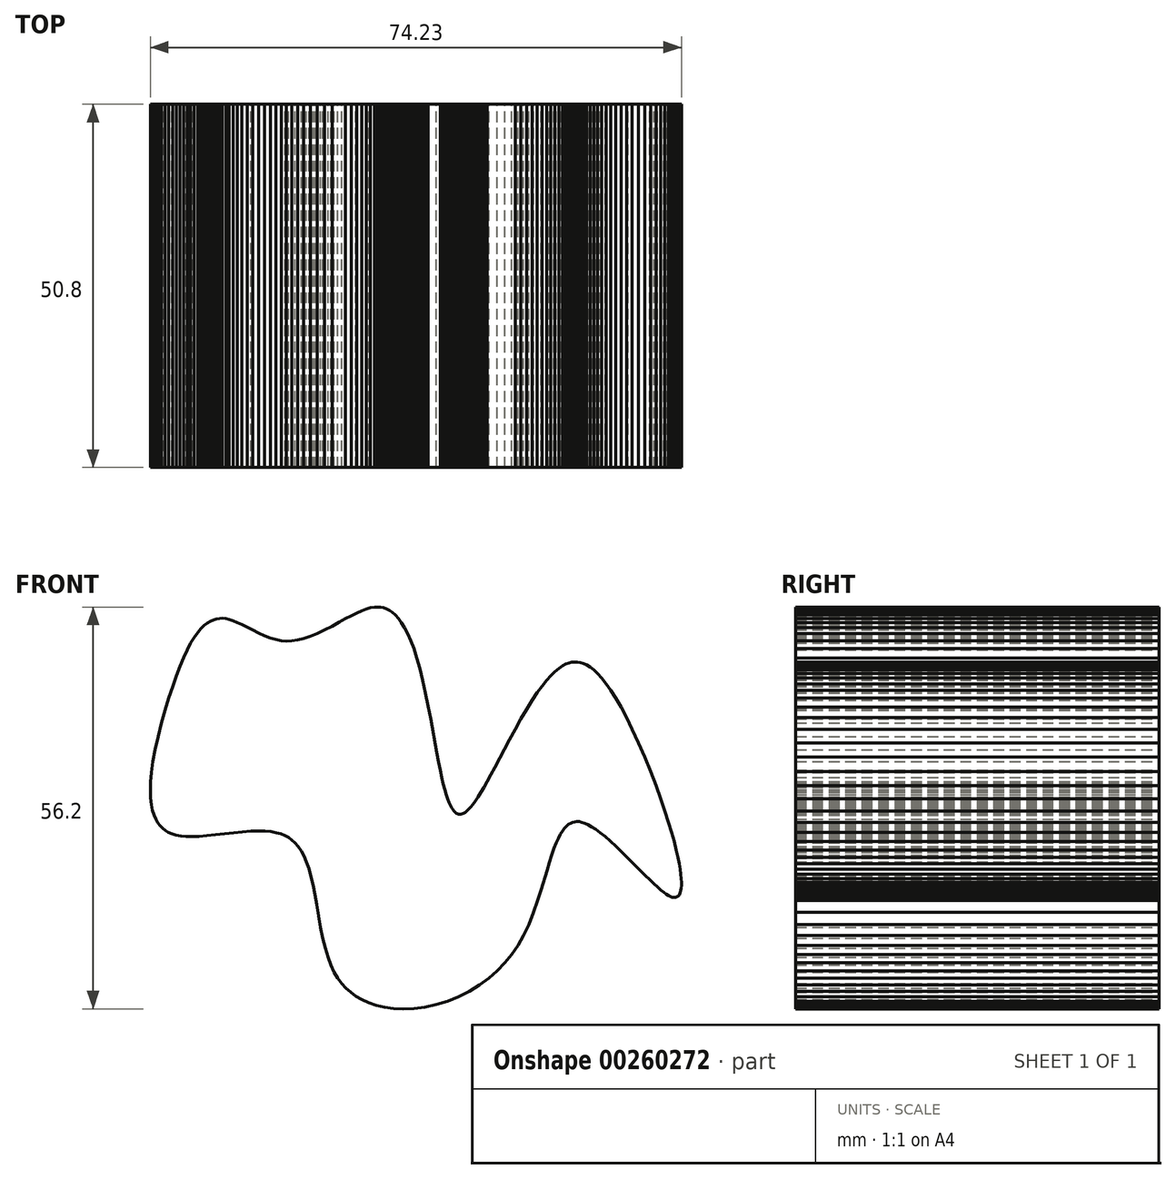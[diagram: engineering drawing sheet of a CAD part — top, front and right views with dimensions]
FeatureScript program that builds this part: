
annotation { "Feature Type Name" : "Feature", "Feature Type Description" : "" }
export const myFeature = defineFeature(function(context is Context, id is Id, definition is map)
    precondition{}
    {
        {
            var Q0;
            Q0=qCreatedBy(makeId("Front.planeOp"),FACE);
            var sketch = newSketch(context, id + "F0", { "sketchPlane" : qUnion([Q0])});
            skLineSegment(sketch, "E0", {"start": v(-36.64, -3.62) * mm, "end": v(-35.67, -3.6) * mm});
            skLineSegment(sketch, "E1", {"start": v(-35.67, -3.6) * mm, "end": v(-34.6, -3.51) * mm});
            skLineSegment(sketch, "E2", {"start": v(-34.6, -3.51) * mm, "end": v(-33.42, -3.4) * mm});
            skLineSegment(sketch, "E3", {"start": v(-33.42, -3.4) * mm, "end": v(-30.87, -3.1) * mm});
            skLineSegment(sketch, "E4", {"start": v(-30.87, -3.1) * mm, "end": v(-29.63, -2.97) * mm});
            skLineSegment(sketch, "E5", {"start": v(-29.63, -2.97) * mm, "end": v(-28.47, -2.89) * mm});
            skLineSegment(sketch, "E6", {"start": v(-28.47, -2.89) * mm, "end": v(-27.42, -2.85) * mm});
            skLineSegment(sketch, "E7", {"start": v(-27.42, -2.85) * mm, "end": v(-26.48, -2.88) * mm});
            skLineSegment(sketch, "E8", {"start": v(-26.48, -2.88) * mm, "end": v(-25.64, -2.96) * mm});
            skLineSegment(sketch, "E9", {"start": v(-25.64, -2.96) * mm, "end": v(-24.9, -3.09) * mm});
            skLineSegment(sketch, "E10", {"start": v(-24.9, -3.09) * mm, "end": v(-24.25, -3.27) * mm});
            skLineSegment(sketch, "E11", {"start": v(-24.25, -3.27) * mm, "end": v(-23.68, -3.5) * mm});
            skLineSegment(sketch, "E12", {"start": v(-23.68, -3.5) * mm, "end": v(-23.18, -3.78) * mm});
            skLineSegment(sketch, "E13", {"start": v(-23.18, -3.78) * mm, "end": v(-22.71, -4.12) * mm});
            skLineSegment(sketch, "E14", {"start": v(-22.71, -4.12) * mm, "end": v(-22.26, -4.53) * mm});
            skLineSegment(sketch, "E15", {"start": v(-22.26, -4.53) * mm, "end": v(-21.84, -5.03) * mm});
            skLineSegment(sketch, "E16", {"start": v(-21.84, -5.03) * mm, "end": v(-21.43, -5.63) * mm});
            skLineSegment(sketch, "E17", {"start": v(-21.43, -5.63) * mm, "end": v(-21.05, -6.34) * mm});
            skLineSegment(sketch, "E18", {"start": v(-21.05, -6.34) * mm, "end": v(-20.69, -7.17) * mm});
            skLineSegment(sketch, "E19", {"start": v(-20.69, -7.17) * mm, "end": v(-20.36, -8.12) * mm});
            skLineSegment(sketch, "E20", {"start": v(-20.36, -8.12) * mm, "end": v(-20.06, -9.2) * mm});
            skLineSegment(sketch, "E21", {"start": v(-20.06, -9.2) * mm, "end": v(-19.78, -10.4) * mm});
            skLineSegment(sketch, "E22", {"start": v(-19.78, -10.4) * mm, "end": v(-19.52, -11.73) * mm});
            skLineSegment(sketch, "E23", {"start": v(-19.52, -11.73) * mm, "end": v(-19.26, -13.17) * mm});
            skLineSegment(sketch, "E24", {"start": v(-19.26, -13.17) * mm, "end": v(-19, -14.74) * mm});
            skLineSegment(sketch, "E25", {"start": v(-19, -14.74) * mm, "end": v(-18.72, -16.33) * mm});
            skLineSegment(sketch, "E26", {"start": v(-18.72, -16.33) * mm, "end": v(-18.4, -17.84) * mm});
            skLineSegment(sketch, "E27", {"start": v(-18.4, -17.84) * mm, "end": v(-18.07, -19.25) * mm});
            skLineSegment(sketch, "E28", {"start": v(-18.07, -19.25) * mm, "end": v(-17.69, -20.5) * mm});
            skLineSegment(sketch, "E29", {"start": v(-17.69, -20.5) * mm, "end": v(-17.27, -21.62) * mm});
            skLineSegment(sketch, "E30", {"start": v(-17.27, -21.62) * mm, "end": v(-16.8, -22.6) * mm});
            skLineSegment(sketch, "E31", {"start": v(-16.8, -22.6) * mm, "end": v(-16.3, -23.45) * mm});
            skLineSegment(sketch, "E32", {"start": v(-16.3, -23.45) * mm, "end": v(-15.77, -24.18) * mm});
            skLineSegment(sketch, "E33", {"start": v(-15.77, -24.18) * mm, "end": v(-15.18, -24.83) * mm});
            skLineSegment(sketch, "E34", {"start": v(-15.18, -24.83) * mm, "end": v(-14.52, -25.42) * mm});
            skLineSegment(sketch, "E35", {"start": v(-14.52, -25.42) * mm, "end": v(-13.77, -25.96) * mm});
            skLineSegment(sketch, "E36", {"start": v(-13.77, -25.96) * mm, "end": v(-12.94, -26.44) * mm});
            skLineSegment(sketch, "E37", {"start": v(-12.94, -26.44) * mm, "end": v(-12, -26.87) * mm});
            skLineSegment(sketch, "E38", {"start": v(-12, -26.87) * mm, "end": v(-10.95, -27.22) * mm});
            skLineSegment(sketch, "E39", {"start": v(-10.95, -27.22) * mm, "end": v(-9.8, -27.5) * mm});
            skLineSegment(sketch, "E40", {"start": v(-9.8, -27.5) * mm, "end": v(-8.53, -27.67) * mm});
            skLineSegment(sketch, "E41", {"start": v(-8.53, -27.67) * mm, "end": v(-7.16, -27.73) * mm});
            skLineSegment(sketch, "E42", {"start": v(-7.16, -27.73) * mm, "end": v(-5.69, -27.67) * mm});
            skLineSegment(sketch, "E43", {"start": v(-5.69, -27.67) * mm, "end": v(-4.15, -27.48) * mm});
            skLineSegment(sketch, "E44", {"start": v(-4.15, -27.48) * mm, "end": v(-2.57, -27.14) * mm});
            skLineSegment(sketch, "E45", {"start": v(-2.57, -27.14) * mm, "end": v(-0.99, -26.65) * mm});
            skLineSegment(sketch, "E46", {"start": v(-0.99, -26.65) * mm, "end": v(0.57, -26.03) * mm});
            skLineSegment(sketch, "E47", {"start": v(0.57, -26.03) * mm, "end": v(2.07, -25.28) * mm});
            skLineSegment(sketch, "E48", {"start": v(2.07, -25.28) * mm, "end": v(3.48, -24.42) * mm});
            skLineSegment(sketch, "E49", {"start": v(3.48, -24.42) * mm, "end": v(4.8, -23.46) * mm});
            skLineSegment(sketch, "E50", {"start": v(4.8, -23.46) * mm, "end": v(5.98, -22.42) * mm});
            skLineSegment(sketch, "E51", {"start": v(5.98, -22.42) * mm, "end": v(7.06, -21.3) * mm});
            skLineSegment(sketch, "E52", {"start": v(7.06, -21.3) * mm, "end": v(8, -20.15) * mm});
            skLineSegment(sketch, "E53", {"start": v(8, -20.15) * mm, "end": v(8.85, -18.89) * mm});
            skLineSegment(sketch, "E54", {"start": v(8.85, -18.89) * mm, "end": v(9.65, -17.46) * mm});
            skLineSegment(sketch, "E55", {"start": v(9.65, -17.46) * mm, "end": v(10.38, -15.92) * mm});
            skLineSegment(sketch, "E56", {"start": v(10.38, -15.92) * mm, "end": v(11.04, -14.24) * mm});
            skLineSegment(sketch, "E57", {"start": v(11.04, -14.24) * mm, "end": v(11.63, -12.57) * mm});
            skLineSegment(sketch, "E58", {"start": v(11.63, -12.57) * mm, "end": v(12.12, -11.04) * mm});
            skLineSegment(sketch, "E59", {"start": v(12.12, -11.04) * mm, "end": v(12.92, -8.36) * mm});
            skLineSegment(sketch, "E60", {"start": v(-3.33, 12.8) * mm, "end": v(-3.67, 14.58) * mm});
            skLineSegment(sketch, "E61", {"start": v(-3.67, 14.58) * mm, "end": v(-4.05, 16.43) * mm});
            skLineSegment(sketch, "E62", {"start": v(-4.05, 16.43) * mm, "end": v(-4.45, 18.24) * mm});
            skLineSegment(sketch, "E63", {"start": v(-4.45, 18.24) * mm, "end": v(-4.85, 19.87) * mm});
            skLineSegment(sketch, "E64", {"start": v(-4.85, 19.87) * mm, "end": v(-5.27, 21.34) * mm});
            skLineSegment(sketch, "E65", {"start": v(-5.27, 21.34) * mm, "end": v(-5.7, 22.63) * mm});
            skLineSegment(sketch, "E66", {"start": v(-5.7, 22.63) * mm, "end": v(-6.12, 23.77) * mm});
            skLineSegment(sketch, "E67", {"start": v(-6.12, 23.77) * mm, "end": v(-6.55, 24.75) * mm});
            skLineSegment(sketch, "E68", {"start": v(-6.55, 24.75) * mm, "end": v(-6.98, 25.58) * mm});
            skLineSegment(sketch, "E69", {"start": v(-6.98, 25.58) * mm, "end": v(-7.4, 26.29) * mm});
            skLineSegment(sketch, "E70", {"start": v(-7.4, 26.29) * mm, "end": v(-7.84, 26.87) * mm});
            skLineSegment(sketch, "E71", {"start": v(-7.84, 26.87) * mm, "end": v(-8.26, 27.35) * mm});
            skLineSegment(sketch, "E72", {"start": v(-8.26, 27.35) * mm, "end": v(-8.68, 27.72) * mm});
            skLineSegment(sketch, "E73", {"start": v(-8.68, 27.72) * mm, "end": v(-9.09, 28) * mm});
            skLineSegment(sketch, "E74", {"start": v(-9.09, 28) * mm, "end": v(-9.5, 28.21) * mm});
            skLineSegment(sketch, "E75", {"start": v(-9.5, 28.21) * mm, "end": v(-9.89, 28.36) * mm});
            skLineSegment(sketch, "E76", {"start": v(-9.89, 28.36) * mm, "end": v(-10.3, 28.44) * mm});
            skLineSegment(sketch, "E77", {"start": v(-10.3, 28.44) * mm, "end": v(-10.73, 28.47) * mm});
            skLineSegment(sketch, "E78", {"start": v(-10.73, 28.47) * mm, "end": v(-11.2, 28.45) * mm});
            skLineSegment(sketch, "E79", {"start": v(-11.2, 28.45) * mm, "end": v(-11.73, 28.35) * mm});
            skLineSegment(sketch, "E80", {"start": v(-11.73, 28.35) * mm, "end": v(-12.31, 28.19) * mm});
            skLineSegment(sketch, "E81", {"start": v(-12.31, 28.19) * mm, "end": v(-12.95, 27.95) * mm});
            skLineSegment(sketch, "E82", {"start": v(-12.95, 27.95) * mm, "end": v(-13.65, 27.65) * mm});
            skLineSegment(sketch, "E83", {"start": v(-13.65, 27.65) * mm, "end": v(-14.42, 27.27) * mm});
            skLineSegment(sketch, "E84", {"start": v(-14.42, 27.27) * mm, "end": v(-15.25, 26.83) * mm});
            skLineSegment(sketch, "E85", {"start": v(-15.25, 26.83) * mm, "end": v(-16.16, 26.33) * mm});
            skLineSegment(sketch, "E86", {"start": v(-16.16, 26.33) * mm, "end": v(-17.12, 25.8) * mm});
            skLineSegment(sketch, "E87", {"start": v(-17.12, 25.8) * mm, "end": v(-18.14, 25.27) * mm});
            skLineSegment(sketch, "E88", {"start": v(-18.14, 25.27) * mm, "end": v(-19.17, 24.77) * mm});
            skLineSegment(sketch, "E89", {"start": v(-19.17, 24.77) * mm, "end": v(-20.15, 24.37) * mm});
            skLineSegment(sketch, "E90", {"start": v(-20.15, 24.37) * mm, "end": v(-21.07, 24.06) * mm});
            skLineSegment(sketch, "E91", {"start": v(-21.07, 24.06) * mm, "end": v(-21.93, 23.85) * mm});
            skLineSegment(sketch, "E92", {"start": v(-21.93, 23.85) * mm, "end": v(-22.74, 23.74) * mm});
            skLineSegment(sketch, "E93", {"start": v(-22.74, 23.74) * mm, "end": v(-23.5, 23.7) * mm});
            skLineSegment(sketch, "E94", {"start": v(-23.5, 23.7) * mm, "end": v(-24.22, 23.77) * mm});
            skLineSegment(sketch, "E95", {"start": v(-24.22, 23.77) * mm, "end": v(-24.96, 23.9) * mm});
            skLineSegment(sketch, "E96", {"start": v(-24.96, 23.9) * mm, "end": v(-25.72, 24.14) * mm});
            skLineSegment(sketch, "E97", {"start": v(-25.72, 24.14) * mm, "end": v(-26.53, 24.45) * mm});
            skLineSegment(sketch, "E98", {"start": v(-26.53, 24.45) * mm, "end": v(-27.37, 24.83) * mm});
            skLineSegment(sketch, "E99", {"start": v(-27.37, 24.83) * mm, "end": v(-28.2, 25.24) * mm});
            skLineSegment(sketch, "E100", {"start": v(-28.2, 25.24) * mm, "end": v(-28.98, 25.65) * mm});
            skLineSegment(sketch, "E101", {"start": v(-28.98, 25.65) * mm, "end": v(-29.7, 26) * mm});
            skLineSegment(sketch, "E102", {"start": v(-29.7, 26) * mm, "end": v(-30.34, 26.3) * mm});
            skLineSegment(sketch, "E103", {"start": v(-30.34, 26.3) * mm, "end": v(-30.94, 26.55) * mm});
            skLineSegment(sketch, "E104", {"start": v(-30.94, 26.55) * mm, "end": v(-31.48, 26.72) * mm});
            skLineSegment(sketch, "E105", {"start": v(-31.48, 26.72) * mm, "end": v(-31.98, 26.84) * mm});
            skLineSegment(sketch, "E106", {"start": v(-31.98, 26.84) * mm, "end": v(-32.43, 26.89) * mm});
            skLineSegment(sketch, "E107", {"start": v(-2.48, 8.11) * mm, "end": v(-3.33, 12.8) * mm});
            skLineSegment(sketch, "E108", {"start": v(5.65, 6.05) * mm, "end": v(5.08, 5) * mm});
            skLineSegment(sketch, "E109", {"start": v(5.08, 5) * mm, "end": v(4.57, 4.06) * mm});
            skLineSegment(sketch, "E110", {"start": v(4.57, 4.06) * mm, "end": v(4.1, 3.23) * mm});
            skLineSegment(sketch, "E111", {"start": v(4.1, 3.23) * mm, "end": v(3.66, 2.5) * mm});
            skLineSegment(sketch, "E112", {"start": v(3.66, 2.5) * mm, "end": v(3.26, 1.88) * mm});
            skLineSegment(sketch, "E113", {"start": v(3.26, 1.88) * mm, "end": v(2.9, 1.34) * mm});
            skLineSegment(sketch, "E114", {"start": v(2.9, 1.34) * mm, "end": v(2.57, 0.89) * mm});
            skLineSegment(sketch, "E115", {"start": v(2.57, 0.89) * mm, "end": v(2.26, 0.5) * mm});
            skLineSegment(sketch, "E116", {"start": v(2.26, 0.5) * mm, "end": v(1.98, 0.2) * mm});
            skLineSegment(sketch, "E117", {"start": v(1.98, 0.2) * mm, "end": v(1.73, -0.04) * mm});
            skLineSegment(sketch, "E118", {"start": v(1.73, -0.04) * mm, "end": v(1.5, -0.23) * mm});
            skLineSegment(sketch, "E119", {"start": v(1.5, -0.23) * mm, "end": v(1.28, -0.36) * mm});
            skLineSegment(sketch, "E120", {"start": v(1.28, -0.36) * mm, "end": v(1.09, -0.45) * mm});
            skLineSegment(sketch, "E121", {"start": v(1.09, -0.45) * mm, "end": v(0.9, -0.5) * mm});
            skLineSegment(sketch, "E122", {"start": v(0.9, -0.5) * mm, "end": v(0.74, -0.52) * mm});
            skLineSegment(sketch, "E123", {"start": v(0.74, -0.52) * mm, "end": v(0.58, -0.5) * mm});
            skLineSegment(sketch, "E124", {"start": v(0.58, -0.5) * mm, "end": v(0.43, -0.46) * mm});
            skLineSegment(sketch, "E125", {"start": v(0.43, -0.46) * mm, "end": v(0.27, -0.38) * mm});
            skLineSegment(sketch, "E126", {"start": v(0.27, -0.38) * mm, "end": v(0.1, -0.26) * mm});
            skLineSegment(sketch, "E127", {"start": v(0.1, -0.26) * mm, "end": v(-0.06, -0.1) * mm});
            skLineSegment(sketch, "E128", {"start": v(-0.06, -0.1) * mm, "end": v(-0.23, 0.13) * mm});
            skLineSegment(sketch, "E129", {"start": v(-0.23, 0.13) * mm, "end": v(-0.4, 0.4) * mm});
            skLineSegment(sketch, "E130", {"start": v(-0.4, 0.4) * mm, "end": v(-0.59, 0.75) * mm});
            skLineSegment(sketch, "E131", {"start": v(-0.59, 0.75) * mm, "end": v(-0.77, 1.16) * mm});
            skLineSegment(sketch, "E132", {"start": v(-0.77, 1.16) * mm, "end": v(-0.96, 1.66) * mm});
            skLineSegment(sketch, "E133", {"start": v(-0.96, 1.66) * mm, "end": v(-1.16, 2.25) * mm});
            skLineSegment(sketch, "E134", {"start": v(-1.16, 2.25) * mm, "end": v(-1.36, 2.93) * mm});
            skLineSegment(sketch, "E135", {"start": v(-1.36, 2.93) * mm, "end": v(-1.56, 3.72) * mm});
            skLineSegment(sketch, "E136", {"start": v(-1.56, 3.72) * mm, "end": v(-1.78, 4.63) * mm});
            skLineSegment(sketch, "E137", {"start": v(-1.78, 4.63) * mm, "end": v(-2, 5.66) * mm});
            skLineSegment(sketch, "E138", {"start": v(-2, 5.66) * mm, "end": v(-2.23, 6.82) * mm});
            skLineSegment(sketch, "E139", {"start": v(-2.23, 6.82) * mm, "end": v(-2.48, 8.11) * mm});
            skLineSegment(sketch, "E140", {"start": v(24.28, -6.68) * mm, "end": v(25.95, -8.37) * mm});
            skLineSegment(sketch, "E141", {"start": v(25.95, -8.37) * mm, "end": v(26.64, -9.06) * mm});
            skLineSegment(sketch, "E142", {"start": v(26.64, -9.06) * mm, "end": v(27.28, -9.69) * mm});
            skLineSegment(sketch, "E143", {"start": v(27.28, -9.69) * mm, "end": v(27.85, -10.23) * mm});
            skLineSegment(sketch, "E144", {"start": v(27.85, -10.23) * mm, "end": v(28.37, -10.7) * mm});
            skLineSegment(sketch, "E145", {"start": v(28.37, -10.7) * mm, "end": v(28.83, -11.1) * mm});
            skLineSegment(sketch, "E146", {"start": v(28.83, -11.1) * mm, "end": v(29.23, -11.42) * mm});
            skLineSegment(sketch, "E147", {"start": v(29.23, -11.42) * mm, "end": v(29.6, -11.68) * mm});
            skLineSegment(sketch, "E148", {"start": v(29.6, -11.68) * mm, "end": v(29.9, -11.87) * mm});
            skLineSegment(sketch, "E149", {"start": v(29.9, -11.87) * mm, "end": v(30.18, -12.01) * mm});
            skLineSegment(sketch, "E150", {"start": v(30.18, -12.01) * mm, "end": v(30.41, -12.1) * mm});
            skLineSegment(sketch, "E151", {"start": v(30.41, -12.1) * mm, "end": v(30.61, -12.15) * mm});
            skLineSegment(sketch, "E152", {"start": v(30.61, -12.15) * mm, "end": v(30.79, -12.16) * mm});
            skLineSegment(sketch, "E153", {"start": v(30.79, -12.16) * mm, "end": v(30.93, -12.14) * mm});
            skLineSegment(sketch, "E154", {"start": v(30.93, -12.14) * mm, "end": v(31.07, -12.1) * mm});
            skLineSegment(sketch, "E155", {"start": v(31.07, -12.1) * mm, "end": v(31.19, -12.03) * mm});
            skLineSegment(sketch, "E156", {"start": v(31.19, -12.03) * mm, "end": v(31.3, -11.93) * mm});
            skLineSegment(sketch, "E157", {"start": v(31.3, -11.93) * mm, "end": v(31.4, -11.8) * mm});
            skLineSegment(sketch, "E158", {"start": v(31.4, -11.8) * mm, "end": v(31.49, -11.64) * mm});
            skLineSegment(sketch, "E159", {"start": v(31.49, -11.64) * mm, "end": v(31.57, -11.43) * mm});
            skLineSegment(sketch, "E160", {"start": v(31.57, -11.43) * mm, "end": v(31.63, -11.17) * mm});
            skLineSegment(sketch, "E161", {"start": v(31.63, -11.17) * mm, "end": v(31.68, -10.85) * mm});
            skLineSegment(sketch, "E162", {"start": v(31.68, -10.85) * mm, "end": v(31.7, -10.48) * mm});
            skLineSegment(sketch, "E163", {"start": v(31.7, -10.48) * mm, "end": v(31.71, -10.03) * mm});
            skLineSegment(sketch, "E164", {"start": v(31.71, -10.03) * mm, "end": v(31.69, -9.52) * mm});
            skLineSegment(sketch, "E165", {"start": v(31.69, -9.52) * mm, "end": v(31.63, -8.91) * mm});
            skLineSegment(sketch, "E166", {"start": v(31.63, -8.91) * mm, "end": v(31.54, -8.22) * mm});
            skLineSegment(sketch, "E167", {"start": v(31.54, -8.22) * mm, "end": v(31.4, -7.43) * mm});
            skLineSegment(sketch, "E168", {"start": v(31.4, -7.43) * mm, "end": v(31.22, -6.52) * mm});
            skLineSegment(sketch, "E169", {"start": v(31.22, -6.52) * mm, "end": v(30.99, -5.5) * mm});
            skLineSegment(sketch, "E170", {"start": v(30.99, -5.5) * mm, "end": v(30.7, -4.35) * mm});
            skLineSegment(sketch, "E171", {"start": v(30.7, -4.35) * mm, "end": v(30.34, -3.06) * mm});
            skLineSegment(sketch, "E172", {"start": v(30.34, -3.06) * mm, "end": v(29.91, -1.63) * mm});
            skLineSegment(sketch, "E173", {"start": v(29.91, -1.63) * mm, "end": v(29.4, -0.06) * mm});
            skLineSegment(sketch, "E174", {"start": v(29.4, -0.06) * mm, "end": v(28.82, 1.65) * mm});
            skLineSegment(sketch, "E175", {"start": v(28.82, 1.65) * mm, "end": v(28.15, 3.49) * mm});
            skLineSegment(sketch, "E176", {"start": v(28.15, 3.49) * mm, "end": v(27.4, 5.46) * mm});
            skLineSegment(sketch, "E177", {"start": v(27.4, 5.46) * mm, "end": v(26.57, 7.48) * mm});
            skLineSegment(sketch, "E178", {"start": v(26.57, 7.48) * mm, "end": v(25.7, 9.48) * mm});
            skLineSegment(sketch, "E179", {"start": v(25.7, 9.48) * mm, "end": v(24.84, 11.36) * mm});
            skLineSegment(sketch, "E180", {"start": v(24.84, 11.36) * mm, "end": v(24.03, 13) * mm});
            skLineSegment(sketch, "E181", {"start": v(24.03, 13) * mm, "end": v(23.27, 14.46) * mm});
            skLineSegment(sketch, "E182", {"start": v(23.27, 14.46) * mm, "end": v(22.54, 15.72) * mm});
            skLineSegment(sketch, "E183", {"start": v(22.54, 15.72) * mm, "end": v(21.86, 16.81) * mm});
            skLineSegment(sketch, "E184", {"start": v(21.86, 16.81) * mm, "end": v(21.2, 17.74) * mm});
            skLineSegment(sketch, "E185", {"start": v(21.2, 17.74) * mm, "end": v(20.6, 18.51) * mm});
            skLineSegment(sketch, "E186", {"start": v(20.6, 18.51) * mm, "end": v(20.01, 19.15) * mm});
            skLineSegment(sketch, "E187", {"start": v(12.92, -8.36) * mm, "end": v(13.27, -7.21) * mm});
            skLineSegment(sketch, "E188", {"start": v(13.27, -7.21) * mm, "end": v(13.6, -6.2) * mm});
            skLineSegment(sketch, "E189", {"start": v(13.6, -6.2) * mm, "end": v(13.9, -5.3) * mm});
            skLineSegment(sketch, "E190", {"start": v(13.9, -5.3) * mm, "end": v(14.2, -4.53) * mm});
            skLineSegment(sketch, "E191", {"start": v(14.2, -4.53) * mm, "end": v(14.5, -3.86) * mm});
            skLineSegment(sketch, "E192", {"start": v(14.5, -3.86) * mm, "end": v(14.8, -3.3) * mm});
            skLineSegment(sketch, "E193", {"start": v(14.8, -3.3) * mm, "end": v(15.09, -2.83) * mm});
            skLineSegment(sketch, "E194", {"start": v(15.09, -2.83) * mm, "end": v(15.38, -2.45) * mm});
            skLineSegment(sketch, "E195", {"start": v(15.38, -2.45) * mm, "end": v(15.66, -2.15) * mm});
            skLineSegment(sketch, "E196", {"start": v(15.66, -2.15) * mm, "end": v(15.94, -1.92) * mm});
            skLineSegment(sketch, "E197", {"start": v(15.94, -1.92) * mm, "end": v(16.23, -1.75) * mm});
            skLineSegment(sketch, "E198", {"start": v(16.23, -1.75) * mm, "end": v(16.5, -1.63) * mm});
            skLineSegment(sketch, "E199", {"start": v(16.5, -1.63) * mm, "end": v(16.8, -1.56) * mm});
            skLineSegment(sketch, "E200", {"start": v(16.8, -1.56) * mm, "end": v(17.1, -1.54) * mm});
            skLineSegment(sketch, "E201", {"start": v(17.1, -1.54) * mm, "end": v(17.42, -1.56) * mm});
            skLineSegment(sketch, "E202", {"start": v(17.42, -1.56) * mm, "end": v(17.8, -1.63) * mm});
            skLineSegment(sketch, "E203", {"start": v(17.8, -1.63) * mm, "end": v(18.2, -1.77) * mm});
            skLineSegment(sketch, "E204", {"start": v(18.2, -1.77) * mm, "end": v(18.66, -1.98) * mm});
            skLineSegment(sketch, "E205", {"start": v(18.66, -1.98) * mm, "end": v(19.18, -2.27) * mm});
            skLineSegment(sketch, "E206", {"start": v(19.18, -2.27) * mm, "end": v(19.74, -2.64) * mm});
            skLineSegment(sketch, "E207", {"start": v(19.74, -2.64) * mm, "end": v(20.37, -3.1) * mm});
            skLineSegment(sketch, "E208", {"start": v(20.37, -3.1) * mm, "end": v(21.05, -3.65) * mm});
            skLineSegment(sketch, "E209", {"start": v(21.05, -3.65) * mm, "end": v(21.78, -4.29) * mm});
            skLineSegment(sketch, "E210", {"start": v(21.78, -4.29) * mm, "end": v(22.57, -5.01) * mm});
            skLineSegment(sketch, "E211", {"start": v(22.57, -5.01) * mm, "end": v(23.4, -5.82) * mm});
            skLineSegment(sketch, "E212", {"start": v(23.4, -5.82) * mm, "end": v(24.28, -6.68) * mm});
            skLineSegment(sketch, "E213", {"start": v(-32.43, 26.89) * mm, "end": v(-32.85, 26.88) * mm});
            skLineSegment(sketch, "E214", {"start": v(-32.85, 26.88) * mm, "end": v(-33.27, 26.81) * mm});
            skLineSegment(sketch, "E215", {"start": v(-33.27, 26.81) * mm, "end": v(-33.68, 26.7) * mm});
            skLineSegment(sketch, "E216", {"start": v(-33.68, 26.7) * mm, "end": v(-34.1, 26.5) * mm});
            skLineSegment(sketch, "E217", {"start": v(-34.1, 26.5) * mm, "end": v(-34.54, 26.24) * mm});
            skLineSegment(sketch, "E218", {"start": v(-34.54, 26.24) * mm, "end": v(-34.98, 25.89) * mm});
            skLineSegment(sketch, "E219", {"start": v(-34.98, 25.89) * mm, "end": v(-35.44, 25.44) * mm});
            skLineSegment(sketch, "E220", {"start": v(-35.44, 25.44) * mm, "end": v(-35.91, 24.88) * mm});
            skLineSegment(sketch, "E221", {"start": v(-35.91, 24.88) * mm, "end": v(-36.39, 24.21) * mm});
            skLineSegment(sketch, "E222", {"start": v(-36.39, 24.21) * mm, "end": v(-36.88, 23.41) * mm});
            skLineSegment(sketch, "E223", {"start": v(-36.88, 23.41) * mm, "end": v(-37.37, 22.48) * mm});
            skLineSegment(sketch, "E224", {"start": v(-37.37, 22.48) * mm, "end": v(-37.87, 21.4) * mm});
            skLineSegment(sketch, "E225", {"start": v(-37.87, 21.4) * mm, "end": v(-38.37, 20.19) * mm});
            skLineSegment(sketch, "E226", {"start": v(-38.37, 20.19) * mm, "end": v(-38.89, 18.83) * mm});
            skLineSegment(sketch, "E227", {"start": v(-38.89, 18.83) * mm, "end": v(-39.4, 17.34) * mm});
            skLineSegment(sketch, "E228", {"start": v(-39.4, 17.34) * mm, "end": v(-39.92, 15.74) * mm});
            skLineSegment(sketch, "E229", {"start": v(-39.92, 15.74) * mm, "end": v(-40.45, 14.04) * mm});
            skLineSegment(sketch, "E230", {"start": v(-40.45, 14.04) * mm, "end": v(-40.95, 12.25) * mm});
            skLineSegment(sketch, "E231", {"start": v(-40.95, 12.25) * mm, "end": v(-41.43, 10.37) * mm});
            skLineSegment(sketch, "E232", {"start": v(-41.43, 10.37) * mm, "end": v(-41.85, 8.53) * mm});
            skLineSegment(sketch, "E233", {"start": v(-41.85, 8.53) * mm, "end": v(-42.16, 6.87) * mm});
            skLineSegment(sketch, "E234", {"start": v(-42.16, 6.87) * mm, "end": v(-42.37, 5.36) * mm});
            skLineSegment(sketch, "E235", {"start": v(-42.37, 5.36) * mm, "end": v(-42.49, 4.01) * mm});
            skLineSegment(sketch, "E236", {"start": v(-42.49, 4.01) * mm, "end": v(-42.52, 2.82) * mm});
            skLineSegment(sketch, "E237", {"start": v(-42.52, 2.82) * mm, "end": v(-42.48, 1.77) * mm});
            skLineSegment(sketch, "E238", {"start": v(-42.48, 1.77) * mm, "end": v(-42.37, 0.84) * mm});
            skLineSegment(sketch, "E239", {"start": v(-42.37, 0.84) * mm, "end": v(-42.2, 0.05) * mm});
            skLineSegment(sketch, "E240", {"start": v(-42.2, 0.05) * mm, "end": v(-42, -0.64) * mm});
            skLineSegment(sketch, "E241", {"start": v(-42, -0.64) * mm, "end": v(-41.74, -1.22) * mm});
            skLineSegment(sketch, "E242", {"start": v(-41.74, -1.22) * mm, "end": v(-41.45, -1.72) * mm});
            skLineSegment(sketch, "E243", {"start": v(-41.45, -1.72) * mm, "end": v(-41.14, -2.13) * mm});
            skLineSegment(sketch, "E244", {"start": v(-41.14, -2.13) * mm, "end": v(-40.8, -2.48) * mm});
            skLineSegment(sketch, "E245", {"start": v(-40.8, -2.48) * mm, "end": v(-40.42, -2.78) * mm});
            skLineSegment(sketch, "E246", {"start": v(-40.42, -2.78) * mm, "end": v(-40, -3.03) * mm});
            skLineSegment(sketch, "E247", {"start": v(-40, -3.03) * mm, "end": v(-39.5, -3.24) * mm});
            skLineSegment(sketch, "E248", {"start": v(-39.5, -3.24) * mm, "end": v(-38.94, -3.41) * mm});
            skLineSegment(sketch, "E249", {"start": v(-38.94, -3.41) * mm, "end": v(-38.27, -3.53) * mm});
            skLineSegment(sketch, "E250", {"start": v(-38.27, -3.53) * mm, "end": v(-37.5, -3.6) * mm});
            skLineSegment(sketch, "E251", {"start": v(-37.5, -3.6) * mm, "end": v(-36.64, -3.62) * mm});
            skLineSegment(sketch, "E252", {"start": v(20.01, 19.15) * mm, "end": v(19.46, 19.66) * mm});
            skLineSegment(sketch, "E253", {"start": v(19.46, 19.66) * mm, "end": v(18.95, 20.06) * mm});
            skLineSegment(sketch, "E254", {"start": v(18.95, 20.06) * mm, "end": v(18.46, 20.36) * mm});
            skLineSegment(sketch, "E255", {"start": v(18.46, 20.36) * mm, "end": v(18.01, 20.57) * mm});
            skLineSegment(sketch, "E256", {"start": v(18.01, 20.57) * mm, "end": v(17.58, 20.7) * mm});
            skLineSegment(sketch, "E257", {"start": v(17.58, 20.7) * mm, "end": v(17.18, 20.78) * mm});
            skLineSegment(sketch, "E258", {"start": v(17.18, 20.78) * mm, "end": v(16.8, 20.79) * mm});
            skLineSegment(sketch, "E259", {"start": v(16.8, 20.79) * mm, "end": v(16.4, 20.75) * mm});
            skLineSegment(sketch, "E260", {"start": v(16.4, 20.75) * mm, "end": v(16, 20.65) * mm});
            skLineSegment(sketch, "E261", {"start": v(16, 20.65) * mm, "end": v(15.56, 20.47) * mm});
            skLineSegment(sketch, "E262", {"start": v(15.56, 20.47) * mm, "end": v(15.09, 20.22) * mm});
            skLineSegment(sketch, "E263", {"start": v(15.09, 20.22) * mm, "end": v(14.59, 19.88) * mm});
            skLineSegment(sketch, "E264", {"start": v(14.59, 19.88) * mm, "end": v(14.05, 19.44) * mm});
            skLineSegment(sketch, "E265", {"start": v(14.05, 19.44) * mm, "end": v(13.48, 18.88) * mm});
            skLineSegment(sketch, "E266", {"start": v(13.48, 18.88) * mm, "end": v(12.87, 18.21) * mm});
            skLineSegment(sketch, "E267", {"start": v(12.87, 18.21) * mm, "end": v(12.23, 17.41) * mm});
            skLineSegment(sketch, "E268", {"start": v(12.23, 17.41) * mm, "end": v(11.55, 16.48) * mm});
            skLineSegment(sketch, "E269", {"start": v(11.55, 16.48) * mm, "end": v(10.83, 15.4) * mm});
            skLineSegment(sketch, "E270", {"start": v(10.83, 15.4) * mm, "end": v(10.08, 14.19) * mm});
            skLineSegment(sketch, "E271", {"start": v(10.08, 14.19) * mm, "end": v(9.28, 12.81) * mm});
            skLineSegment(sketch, "E272", {"start": v(9.28, 12.81) * mm, "end": v(8.47, 11.37) * mm});
            skLineSegment(sketch, "E273", {"start": v(8.47, 11.37) * mm, "end": v(7.68, 9.9) * mm});
            skLineSegment(sketch, "E274", {"start": v(7.68, 9.9) * mm, "end": v(5.65, 6.05) * mm});
            skSolve(sketch);
        }
        {
            var Q0;
            Q0=makeQuery(id+"F0.imprint","IMPRINT",FACE,{"disambiguationData":[TD([[makeQuery(id+"F0.imprint","IMPRINT",EDGE,{"derivedFrom":sQuery(id+"F0.wireOp",EDGE,"E0")}),1.0]])]});
            extrude(context, id + "F1", {"entities" : qUnion([Q0]), "endBound" : BoundingType.SYMMETRIC, "depth" : 50.8 * mm});
        }
    });
